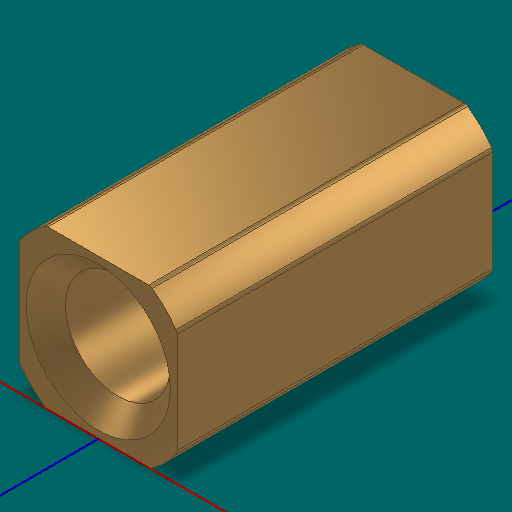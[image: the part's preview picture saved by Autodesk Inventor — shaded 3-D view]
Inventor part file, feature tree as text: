
AUTODESK INVENTOR PART (.ipt)
format: ipt  version: 2025 (Build 290162000, 162)  size: 167,424 bytes
history: native  units: in
note: dims shown in document units (in); Inventor stores cm internally (conversion verified against a paired STEP export)
features: other x3, sketch x2
ambient origin geometry x8: Origin, YZ Plane, XZ Plane, XY Plane, X Axis, Y Axis, Z Axis, Center Point
bodies: Solid1 (feature_tree)
feature tree (5):
  other  "HS Shaft Adapter Circle_mirrored.ipt"
  other  "Solid1::HS Shaft Adapter Circle_mirrored.ipt"
  other  "TaggingFeature1"
  sketch  "Sketch1"  dims[d0=0.3937in]
  sketch  "Sketch2"
